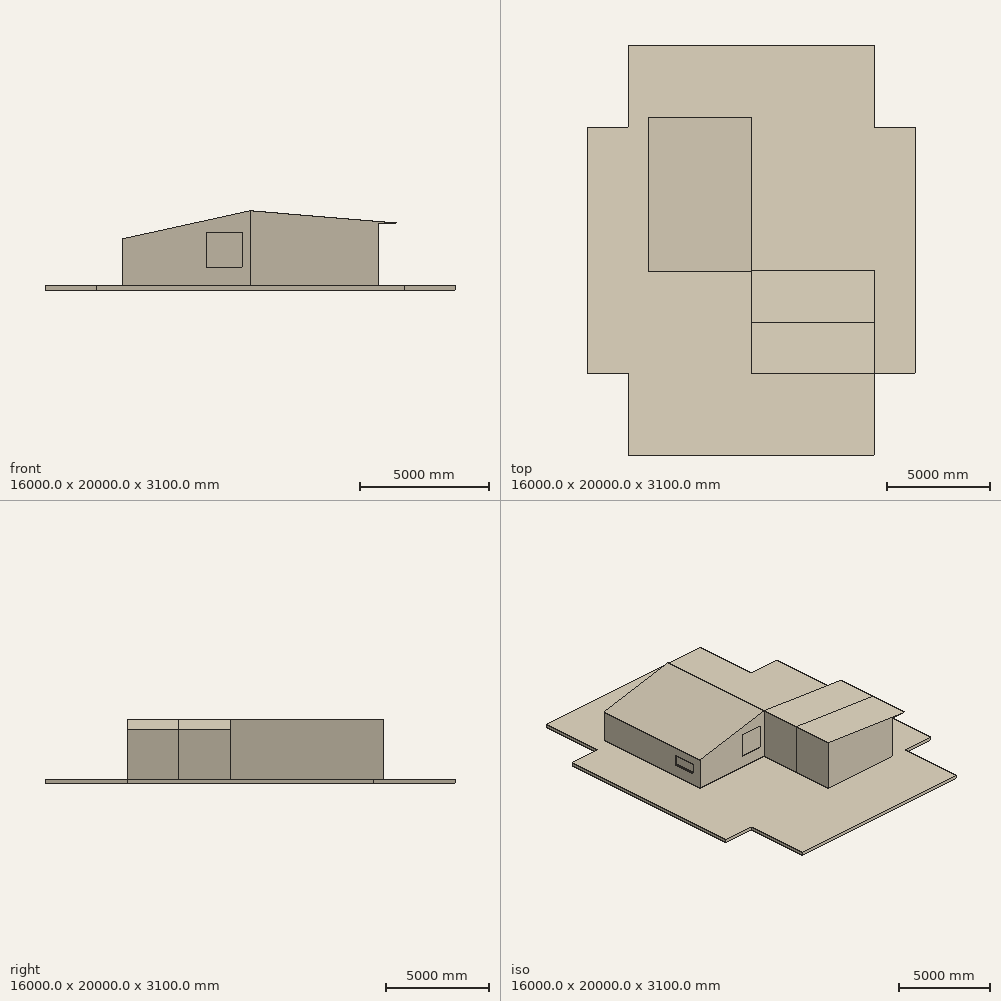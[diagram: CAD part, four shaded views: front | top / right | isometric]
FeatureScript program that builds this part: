
annotation { "Feature Type Name" : "Feature", "Feature Type Description" : "" }
export const myFeature = defineFeature(function(context is Context, id is Id, definition is map)
    precondition{}
    {
        {
            var Q0;
            Q0=qCreatedBy(makeId("Front.planeOp"),FACE);
            var sketch = newSketch(context, id + "F0", { "sketchPlane" : qUnion([Q0])});
            skLineSegment(sketch, "E0", {"start": v(0, 0) * mm, "end": v(0, 2900) * mm});
            skLineSegment(sketch, "E1", {"start": v(0, 0) * mm, "end": v(5000, 0) * mm});
            skLineSegment(sketch, "E2", {"start": v(5000, 0) * mm, "end": v(5000, 2400) * mm});
            skLineSegment(sketch, "E3", {"start": v(0, 2400) * mm, "end": v(5979.13, 2400) * mm});
            skLineSegment(sketch, "E4", {"start": v(0, 2900) * mm, "end": v(5979.13, 2400) * mm});
            skLineSegment(sketch, "E5", {"start": v(1250, 2400) * mm, "end": v(1250, 2795.47) * mm});
            skLineSegment(sketch, "E6", {"start": v(2500, 2690.94) * mm, "end": v(2500, 2400) * mm});
            skLineSegment(sketch, "E7", {"start": v(3750, 2586.4) * mm, "end": v(3750, 2400) * mm});
            skLineSegment(sketch, "E8", {"start": v(0, 2400) * mm, "end": v(1250, 2795.47) * mm});
            skLineSegment(sketch, "E9", {"start": v(1250, 2400) * mm, "end": v(2500, 2690.94) * mm});
            skLineSegment(sketch, "E10", {"start": v(2500, 2400) * mm, "end": v(3750, 2586.4) * mm});
            skPoint(sketch, "E11.MirrorCS.end.orphan", {"position": v(-5979.13, 2400) * mm});
            skPoint(sketch, "E11.MirrorCS.start.orphan", {"position": v(0, 2900) * mm});
            skPoint(sketch, "E12.MirrorCS.start.orphan", {"position": v(0, 2400) * mm});
            skLineSegment(sketch, "E13", {"start": v(0, 0) * mm, "end": v(-5100, 0) * mm});
            skLineSegment(sketch, "E14", {"start": v(-5100, 0) * mm, "end": v(-5100, 1740) * mm});
            skLineSegment(sketch, "E15", {"start": v(-5100, 1740) * mm, "end": v(0, 2900) * mm});
            skLineSegment(sketch, "E16", {"start": v(-5100, 1740) * mm, "end": v(0, 2400) * mm});
            skLineSegment(sketch, "E17", {"start": v(-1239.66, 2239.57) * mm, "end": v(-1287.24, 2607.22) * mm});
            skLineSegment(sketch, "E18.0", {"start": v(-2479.33, 2079.15) * mm, "end": v(-2511.62, 2328.73) * mm});
            skLineSegment(sketch, "E19.0", {"start": v(-3718.99, 1918.72) * mm, "end": v(-3736, 2050.24) * mm});
            skLineSegment(sketch, "E20", {"start": v(0, 2400) * mm, "end": v(-1287.24, 2607.22) * mm});
            skLineSegment(sketch, "E21", {"start": v(-1239.66, 2239.57) * mm, "end": v(-2511.62, 2328.73) * mm});
            skLineSegment(sketch, "E22", {"start": v(-2479.33, 2079.15) * mm, "end": v(-3736, 2050.24) * mm});
            skLineSegment(sketch, "E23", {"start": v(-5100, 1740) * mm, "end": v(0, 1740) * mm});
            skSolve(sketch);
        }
        {
            var Q0;
            Q0=qCreatedBy(makeId("Front.planeOp"),FACE);
            cPlane(context, id + "F1", {"entities" : qUnion([Q0]), "cplaneType" : CPlaneType.OFFSET, "offset" : 13000 * mm, "width" : 150 * mm, "height" : 150 * mm});
        }
        {
            var Q0;
            Q0=qCreatedBy(id+"F1.planeOp",FACE);
            var sketch = newSketch(context, id + "F2", { "sketchPlane" : qUnion([Q0])});
            skLineSegment(sketch, "E24.0", {"start": v(0, 0) * mm, "end": v(0, 2900) * mm});
            skLineSegment(sketch, "E24.1", {"start": v(0, 2900) * mm, "end": v(5979.13, 2400) * mm});
            skLineSegment(sketch, "E24.2", {"start": v(0, 0) * mm, "end": v(5000, 0) * mm});
            skLineSegment(sketch, "E24.3", {"start": v(5000, 0) * mm, "end": v(5000, 2400) * mm});
            skLineSegment(sketch, "E24.4", {"start": v(0, 2400) * mm, "end": v(5979.13, 2400) * mm});
            skLineSegment(sketch, "E25.0", {"start": v(0, 0) * mm, "end": v(-5000, 0) * mm});
            skPoint(sketch, "E25.3.start.orphan", {"position": v(0, 2900) * mm});
            skPoint(sketch, "E26.orphan", {"position": v(0, 2400) * mm});
            skPoint(sketch, "E25.1.start.orphan", {"position": v(-5000, 0) * mm});
            skLineSegment(sketch, "E27", {"start": v(-5000, 0) * mm, "end": v(-5000, 1800) * mm});
            skLineSegment(sketch, "E28", {"start": v(-5000, 1800) * mm, "end": v(0, 2900) * mm});
            skSolve(sketch);
        }
        {
            var Q0;
            {var subQ0=sQuery(id+"F2.wireOp",EDGE,"E24.2");Q0=makeQuery(id+"F2.imprint","IMPRINT",FACE,{"disambiguationData":[TD([[makeQuery(id+"F2.imprint","IMPRINT",EDGE,{"derivedFrom":subQ0}),1.0]])]});}
            var Q1;
            {var subQ0=sQuery(id+"F2.wireOp",EDGE,"E24.1");Q1=makeQuery(id+"F2.imprint","IMPRINT",FACE,{"disambiguationData":[TD([[makeQuery(id+"F2.imprint","IMPRINT",EDGE,{"derivedFrom":subQ0}),-1.0]])]});}
            extrude(context, id + "F3", {"entities" : qUnion([Q0, Q1]), "depth" : 2500 * mm, "offsetDistance" : 25 * mm});
        }
        {
            var Q0;
            Q0=makeQuery(id+"F3.opExtrude","CAP_FACE",FACE,{"disambiguationData":[OSD([sQuery(id+"F2.wireOp",EDGE,"E24.0"),sQuery(id+"F2.wireOp",EDGE,"E24.1"),sQuery(id+"F2.wireOp",EDGE,"E24.2"),sQuery(id+"F2.wireOp",EDGE,"E24.3"),sQuery(id+"F2.wireOp",EDGE,"E24.4")])],"isStart":false});
            extrude(context, id + "F4", {"entities" : qUnion([Q0]), "depth" : 2500 * mm, "offsetDistance" : 25 * mm});
        }
        {
            var Q0;
            {var subQ0=sQuery(id+"F2.wireOp",EDGE,"E25.0");Q0=makeQuery(id+"F2.imprint","IMPRINT",FACE,{"disambiguationData":[TD([[makeQuery(id+"F2.imprint","IMPRINT",EDGE,{"derivedFrom":subQ0}),-1.0]])]});}
            var Q1;
            {var subQ0=sQuery(id+"F2.wireOp",EDGE,"E25.3");Q1=makeQuery(id+"F2.imprint","IMPRINT",FACE,{"disambiguationData":[TD([[makeQuery(id+"F2.imprint","IMPRINT",EDGE,{"derivedFrom":subQ0}),1.0]])]});}
            extrude(context, id + "F5", {"entities" : qUnion([Q0, Q1]), "oppositeDirection" : true, "depth" : 7500 * mm, "offsetDistance" : 25 * mm});
        }
        {
            var Q0;
            Q0=qCreatedBy(makeId("Top.planeOp"),FACE);
            var sketch = newSketch(context, id + "F6", { "sketchPlane" : qUnion([Q0])});
            skLineSegment(sketch, "E29.bottom", {"start": v(-8000, -6000) * mm, "end": v(8000, -6000) * mm});
            skLineSegment(sketch, "E29.top", {"start": v(-8000, -18000) * mm, "end": v(8000, -18000) * mm});
            skLineSegment(sketch, "E29.left", {"start": v(-8000, -6000) * mm, "end": v(-8000, -18000) * mm});
            skLineSegment(sketch, "E29.right", {"start": v(8000, -6000) * mm, "end": v(8000, -18000) * mm});
            skLineSegment(sketch, "E30.bottom", {"start": v(-6000, -18000) * mm, "end": v(6000, -18000) * mm});
            skLineSegment(sketch, "E30.top", {"start": v(-6000, -22000) * mm, "end": v(6000, -22000) * mm});
            skLineSegment(sketch, "E30.left", {"start": v(-6000, -18000) * mm, "end": v(-6000, -22000) * mm});
            skLineSegment(sketch, "E30.right", {"start": v(6000, -18000) * mm, "end": v(6000, -22000) * mm});
            skLineSegment(sketch, "E31.bottom", {"start": v(-6000, -6000) * mm, "end": v(6000, -6000) * mm});
            skLineSegment(sketch, "E31.top", {"start": v(-6000, -2000) * mm, "end": v(6000, -2000) * mm});
            skLineSegment(sketch, "E31.left", {"start": v(-6000, -6000) * mm, "end": v(-6000, -2000) * mm});
            skLineSegment(sketch, "E31.right", {"start": v(6000, -6000) * mm, "end": v(6000, -2000) * mm});
            skSolve(sketch);
        }
        {
            var Q0;
            Q0=makeQuery(id+"F6.imprint","IMPRINT",FACE,{"disambiguationData":[TD([[makeQuery(id+"F6.imprint","IMPRINT",EDGE,{"derivedFrom":sQuery(id+"F6.wireOp",EDGE,"E30.top")}),1.0]])]});
            var Q1;
            {var subQ5=sQuery(id+"F6.wireOp",EDGE,"E29.left");Q1=makeQuery(id+"F6.imprint","IMPRINT",FACE,{"disambiguationData":[TD([[makeQuery(id+"F6.imprint","IMPRINT",EDGE,{"derivedFrom":subQ5}),1.0]])]});}
            var Q2;
            Q2=makeQuery(id+"F6.imprint","IMPRINT",FACE,{"disambiguationData":[TD([[makeQuery(id+"F6.imprint","IMPRINT",EDGE,{"derivedFrom":sQuery(id+"F6.wireOp",EDGE,"E31.top")}),-1.0]])]});
            extrude(context, id + "F7", {"entities" : qUnion([Q0, Q1, Q2]), "oppositeDirection" : true, "depth" : 200 * mm, "offsetDistance" : 25 * mm});
        }
        {
            var Q0;
            Q0=makeQuery(id+"F5.opExtrude","SWEPT_FACE",FACE,{"disambiguationData":[OSD([sQuery(id+"F2.wireOp",EDGE,"E27")])]});
            var sketch = newSketch(context, id + "F8", { "sketchPlane" : qUnion([Q0])});
            skLineSegment(sketch, "E32.0", {"start": v(13000, 0) * mm, "end": v(13000, 1800) * mm});
            skLineSegment(sketch, "E33.0", {"start": v(10500, 0) * mm, "end": v(10500, 1800) * mm});
            skLineSegment(sketch, "E34.bottom", {"start": v(11050, 1300) * mm, "end": v(12450, 1300) * mm});
            skLineSegment(sketch, "E34.top", {"start": v(11050, 700) * mm, "end": v(12450, 700) * mm});
            skLineSegment(sketch, "E34.left", {"start": v(11050, 1300) * mm, "end": v(11050, 700) * mm});
            skLineSegment(sketch, "E34.right", {"start": v(12450, 1300) * mm, "end": v(12450, 700) * mm});
            skLineSegment(sketch, "E35", {"start": v(11750, 1300) * mm, "end": v(11750, 700) * mm});
            skSolve(sketch);
        }
        {
            var Q0;
            {var subQ0=sQuery(id+"F8.wireOp",EDGE,"E34.left");Q0=makeQuery(id+"F8.imprint","IMPRINT",FACE,{"disambiguationData":[TD([[makeQuery(id+"F8.imprint","IMPRINT",EDGE,{"derivedFrom":subQ0}),1.0]])]});}
            var Q1;
            {var subQ0=sQuery(id+"F8.wireOp",EDGE,"E34.right");Q1=makeQuery(id+"F8.imprint","IMPRINT",FACE,{"disambiguationData":[TD([[makeQuery(id+"F8.imprint","IMPRINT",EDGE,{"derivedFrom":subQ0}),-1.0]])]});}
            extrude(context, id + "F9", {"entities" : qUnion([Q0, Q1]), "operationType" : NewBodyOperationType.REMOVE, "oppositeDirection" : true, "depth" : 100 * mm, "offsetDistance" : 25 * mm});
        }
        {
            var Q0;
            Q0=makeQuery(id+"F5.opExtrude","CAP_FACE",FACE,{"disambiguationData":[OSD([sQuery(id+"F2.wireOp",EDGE,"E24.0"),sQuery(id+"F2.wireOp",EDGE,"E25.0"),sQuery(id+"F2.wireOp",EDGE,"E27"),sQuery(id+"F2.wireOp",EDGE,"E28")])],"isStart":true});
            var sketch = newSketch(context, id + "F10", { "sketchPlane" : qUnion([Q0])});
            skLineSegment(sketch, "E36.bottom", {"start": v(-1700, 2050) * mm, "end": v(-300, 2050) * mm});
            skLineSegment(sketch, "E36.top", {"start": v(-1700, 700) * mm, "end": v(-300, 700) * mm});
            skLineSegment(sketch, "E36.left", {"start": v(-1700, 2050) * mm, "end": v(-1700, 700) * mm});
            skLineSegment(sketch, "E36.right", {"start": v(-300, 2050) * mm, "end": v(-300, 700) * mm});
            skLineSegment(sketch, "E37", {"start": v(-1000, 2050) * mm, "end": v(-1000, 700) * mm});
            skSolve(sketch);
        }
        {
            var Q0;
            {var subQ0=sQuery(id+"F10.wireOp",EDGE,"E36.left");Q0=makeQuery(id+"F10.imprint","IMPRINT",FACE,{"disambiguationData":[TD([[makeQuery(id+"F10.imprint","IMPRINT",EDGE,{"derivedFrom":subQ0}),1.0]])]});}
            var Q1;
            {var subQ0=sQuery(id+"F10.wireOp",EDGE,"E36.right");Q1=makeQuery(id+"F10.imprint","IMPRINT",FACE,{"disambiguationData":[TD([[makeQuery(id+"F10.imprint","IMPRINT",EDGE,{"derivedFrom":subQ0}),-1.0]])]});}
            extrude(context, id + "F11", {"entities" : qUnion([Q0, Q1]), "operationType" : NewBodyOperationType.REMOVE, "oppositeDirection" : true, "depth" : 25 * mm, "offsetDistance" : 25 * mm});
        }
    });
